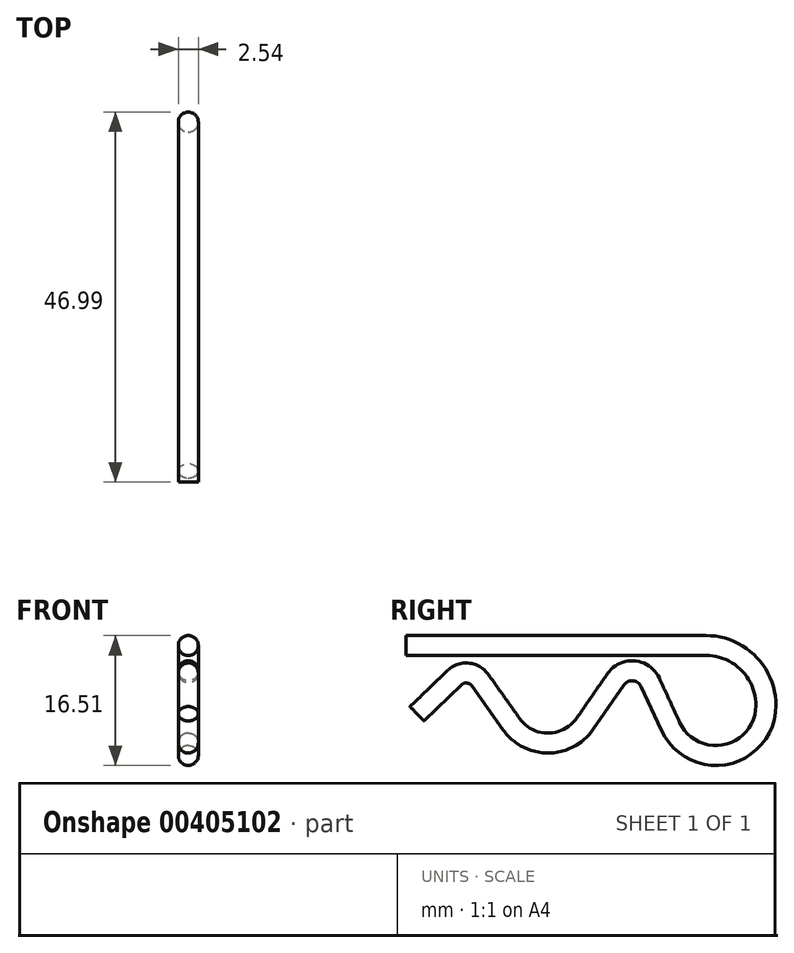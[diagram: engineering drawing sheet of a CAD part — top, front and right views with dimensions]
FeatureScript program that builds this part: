
annotation { "Feature Type Name" : "Feature", "Feature Type Description" : "" }
export const myFeature = defineFeature(function(context is Context, id is Id, definition is map)
    precondition{}
    {
        {
            var Q0;
            Q0=qCreatedBy(makeId("Right.planeOp"),FACE);
            var sketch = newSketch(context, id + "F0", { "sketchPlane" : qUnion([Q0])});
            skLineSegment(sketch, "E0", {"start": v(0, 7.94) * mm, "end": v(38.1, 7.94) * mm});
            skArc(sketch, "E1", {"start": v(45.72, 0.32) * mm, "mid": v(43.49, 5.7) * mm, "end": v(38.1, 7.94) * mm});
            skArc(sketch, "E2", {"start": v(33.6, -2.34) * mm, "mid": v(40.73, -5.89) * mm, "end": v(45.72, 0.32) * mm});
            skLineSegment(sketch, "E3", {"start": v(1.4, -0.73) * mm, "end": v(6.14, 3.84) * mm});
            skArc(sketch, "E4", {"start": v(9.42, 3.54) * mm, "mid": v(7.85, 4.44) * mm, "end": v(6.14, 3.84) * mm});
            skLineSegment(sketch, "E5", {"start": v(9.42, 3.54) * mm, "end": v(13.39, -2.05) * mm});
            skArc(sketch, "E6", {"start": v(13.39, -2.05) * mm, "mid": v(18.07, -4.46) * mm, "end": v(22.73, -2) * mm});
            skLineSegment(sketch, "E7", {"start": v(22.73, -2) * mm, "end": v(26.65, 3.65) * mm});
            skLineSegment(sketch, "E8", {"start": v(33.6, -2.34) * mm, "end": v(31.02, 3.27) * mm});
            skArc(sketch, "E9", {"start": v(31.02, 3.27) * mm, "mid": v(28.95, 4.73) * mm, "end": v(26.65, 3.65) * mm});
            skSolve(sketch);
        }
        {
            var Q0;
            Q0=qCreatedBy(makeId("Front.planeOp"),FACE);
            var sketch = newSketch(context, id + "F1", { "sketchPlane" : qUnion([Q0])});
            skPoint(sketch, "E10.0", {"position": v(0, 7.94) * mm});
            skCircle(sketch, "E11", {"center": v(0, 7.94) * mm, "radius": 1.27 * mm});
            skSolve(sketch);
        }
        {
            var Q0;
            Q0 = qSketchRegion(id + "F1", true);
            var Q1;
            Q1 = qConstructionFilter(qBodyType(qCreatedBy(id + "F0" ,EDGE), BodyType.WIRE), ConstructionObject.NO);
            sweep(context, id + "F2", {"profiles" : qUnion([Q0]), "path" : qUnion([Q1])});
        }
    });
